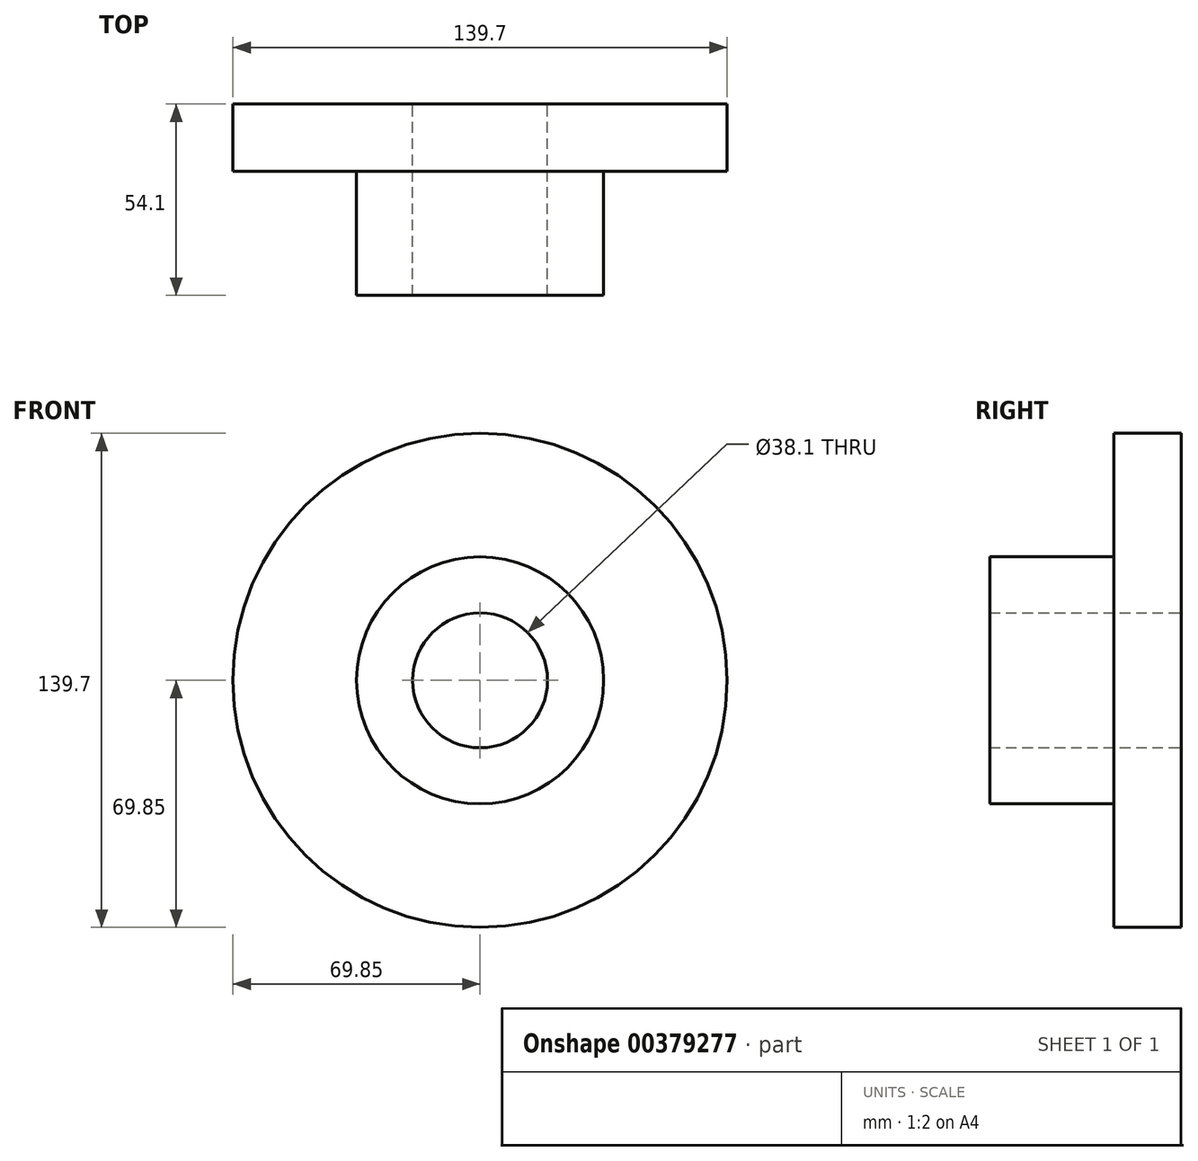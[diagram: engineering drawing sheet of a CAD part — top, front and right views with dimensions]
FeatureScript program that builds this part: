
annotation { "Feature Type Name" : "Feature", "Feature Type Description" : "" }
export const myFeature = defineFeature(function(context is Context, id is Id, definition is map)
    precondition{}
    {
        {
            var Q0;
            Q0=qCreatedBy(makeId("Top.planeOp"),FACE);
            var sketch = newSketch(context, id + "F0", { "sketchPlane" : qUnion([Q0])});
            skLineSegment(sketch, "E0", {"start": v(0, 0) * mm, "end": v(0, -63.61) * mm, "construction": true});
            skLineSegment(sketch, "E1", {"start": v(19.05, 0) * mm, "end": v(19.05, -54.1) * mm});
            skLineSegment(sketch, "E2", {"start": v(19.05, -54.1) * mm, "end": v(34.93, -54.1) * mm});
            skLineSegment(sketch, "E3", {"start": v(34.93, -54.1) * mm, "end": v(34.93, -19.05) * mm});
            skLineSegment(sketch, "E4", {"start": v(34.93, -19.05) * mm, "end": v(69.85, -19.05) * mm});
            skLineSegment(sketch, "E5", {"start": v(69.85, -19.05) * mm, "end": v(69.85, 0) * mm});
            skLineSegment(sketch, "E6", {"start": v(69.85, 0) * mm, "end": v(19.05, 0) * mm});
            skSolve(sketch);
        }
        {
            var Q0;
            Q0=makeQuery(id+"F0.imprint","IMPRINT",FACE,{"disambiguationData":[TD([[makeQuery(id+"F0.imprint","IMPRINT",EDGE,{"derivedFrom":sQuery(id+"F0.wireOp",EDGE,"E1")}),1.0]])]});
            var Q1;
            Q1=sQuery(id+"F0.wireOp",EDGE,"E0");
            revolve(context, id + "F1", {"entities" : qUnion([Q0]), "axis" : qUnion([Q1]), "revolveType" : RevolveType.FULL});
        }
        {
            var Q0;
            Q0=qCreatedBy(makeId("Front.planeOp"),FACE);
            var sketch = newSketch(context, id + "F2", { "sketchPlane" : qUnion([Q0])});
            skCircle(sketch, "E7", {"center": v(0, 0) * mm, "radius": 53.98 * mm, "construction": true});
            skCircle(sketch, "E8", {"center": v(53.98, 0) * mm, "radius": 6.35 * mm});
            skSolve(sketch);
        }
        {
            var Q0;
            Q0 = qSketchRegion(id + "F2", true);
            extrude(context, id + "F3", {"entities" : qUnion([Q0]), "operationType" : NewBodyOperationType.REMOVE, "oppositeDirection" : true, "depth" : 25.4 * mm});
        }
    });
